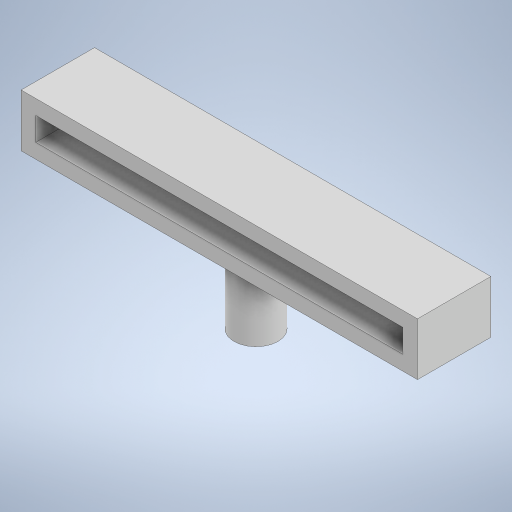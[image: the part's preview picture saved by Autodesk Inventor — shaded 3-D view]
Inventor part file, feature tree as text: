
AUTODESK INVENTOR PART (.ipt)
format: ipt  version: 2023 (Build 270158000, 158)  size: 233,472 bytes
history: native  units: mm
features: extrude x2, sketch x2
ambient origin geometry x8: Origin, YZ Plane, XZ Plane, XY Plane, X Axis, Y Axis, Z Axis, Center Point
bodies: Solid1 (feature_tree)
feature tree (4):
  extrude  "Extrusion1"  Depth=6.35mm
  extrude  "Extrusion2"  Depth=20.0mm TaperAngle=0.0deg
  sketch  "Sketch1"  dims[d0=100.0mm d1=6.35mm]
  sketch  "Sketch2"  dims[d2=4.0mm d3=20.0mm d4=0.0mm d5=12.0mm d6=20.0mm d7=0.0mm]
